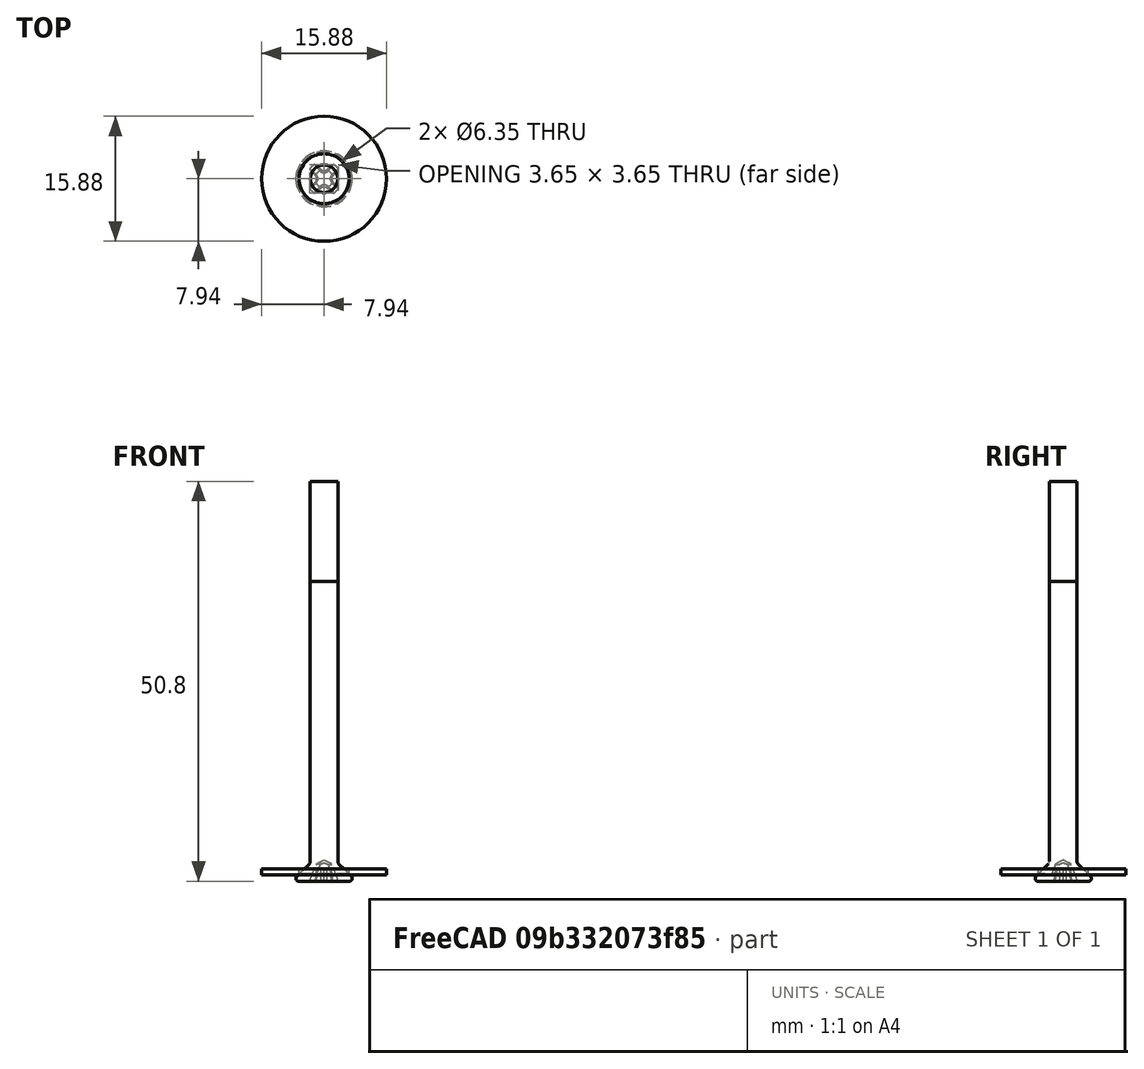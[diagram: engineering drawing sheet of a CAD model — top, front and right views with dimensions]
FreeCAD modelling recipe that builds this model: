
FCSTD DOCUMENT  (FreeCAD 0.19R)
Label: Fasteners
License: Creative Commons Attribution
LicenseURL: http://creativecommons.org/licenses/by/4.0/
objects: Part::Cylinder×4, Part::FeaturePython×2, Part::Cut×2, Part::Fillet×2, Part::MultiFuse×2
note: 12 computed .brp shape members not serialized (recipe doc carries the construction recipe); baked Part::Feature solids carry a one-line shape summary decoded from their .brp

FEATURE [Part::FeaturePython] Screw  label="(M3.5)x38.1-Screw"  # Fasteners workbench fastener (typed FeaturePython)
  Placement = pos=(0,0,-1.5875) rot=(0,1,0;3.14159rad)
  diameter = 5
  invert = false
  length = 11
  lengthCustom = 38.1
  matchOuter = false
  offset = 0
  thread = false
  type = 34
FEATURE [Part::Cylinder] Cylinder
  Angle = 360
  AttacherType = Attacher::AttachEngine3D
  Height = 0.8
  Radius = 7.9375
FEATURE [Part::Cylinder] Cylinder001
  Angle = 360
  AttacherType = Attacher::AttachEngine3D
  Height = 6.35
  Placement = pos=(0,0,-1.5875) rot=(0,0,1;0rad)
  Radius = 3.175
FEATURE [Part::Cut] Cut  label="1/4x5/8_Washer"
  Base = -> Cylinder
  Placement = pos=(0,0,-0.79375) rot=(0,0,1;0rad)
  Tool = -> Cylinder001
FEATURE [Part::Fillet] Fillet  label="#8x1-1/2_flat-head_Screw"
  Base = -> Screw
  Edges = 2 edges r=0.3: [Edge1,Edge2]
FEATURE [Part::MultiFuse] Fusion  label="Screw_Washer_A"
  Shapes = -> [Cut,Fillet]
FEATURE [Part::FeaturePython] Screw001  label="(M3.5)x50.8-Screw"  # Fasteners workbench fastener (typed FeaturePython)
  Placement = pos=(0,0,-1.5875) rot=(0,1,0;3.14159rad)
  diameter = 5
  invert = false
  length = 11
  lengthCustom = 50.8
  matchOuter = false
  offset = 0
  thread = false
  type = 34
FEATURE [Part::Cylinder] Cylinder002
  Angle = 360
  AttacherType = Attacher::AttachEngine3D
  Height = 0.8
  Radius = 7.9375
FEATURE [Part::Cylinder] Cylinder003
  Angle = 360
  AttacherType = Attacher::AttachEngine3D
  Height = 6.35
  Placement = pos=(0,0,-1.5875) rot=(0,0,1;0rad)
  Radius = 3.175
FEATURE [Part::Cut] Cut001  label="1/4x5/8_Washer001"
  Base = -> Cylinder002
  Placement = pos=(0,0,-0.79375) rot=(0,0,1;0rad)
  Tool = -> Cylinder003
FEATURE [Part::Fillet] Fillet001  label="#8x2_flat-head_Screw"
  Base = -> Screw001
  Edges = 2 edges r=0.3: [Edge1,Edge2]
FEATURE [Part::MultiFuse] Fusion001  label="Screw_Washer_B"
  Shapes = -> [Cut001,Fillet001]
